# Revit family: A172408F-BF12-BCD
name_source: partatom
category: Mechanical Equipment
revit_build: Autodesk Revit MEP 2016 (Build: 20150220_1215(x64)
units: mm (PartAtom-declared; Revit-internal decimal feet)

## family parameters
Cut with Voids When Loaded = No
Host = Face
OmniClass Number = 23.65.70.14.11
OmniClass Title = Drinking Fountains/Coolers
Part Type = Normal
Room Calculation Point = No
Round Connector Dimension = Use Diameter
Shared = Yes

## types (1)
- A172408F-BF12-BCD
    A172408F-BF12-BCD - H2O To Go Bottle Filler, Cooler Mount = Yes
    Amperage = 0
    CW Connection = Yes
    Default Elevation = 31.625 "
    Description = H2O To Go Bottle Filler, Cooler Mount
    HW Connection = No
    Manufacturer = Murdock
    Material = Stainless Steel
    Model = A172408F-BF12-BCD
    OVERALL DEPTH = 18.5
    OVERALL SIZE HEIGHT = 50.625
    OVERALL SIZE WIDTH = 37.125
    Revised Date = 06/20/18
    Tempered Water Connection = No
    URL = https://www.murdockmfg.com
    Vent Connection = No
    Voltage = 0
    Waste Connection = Yes

## geometry (parser evidence)
native form markers: Sweep x10
no freeform markers — native parametric forms only
